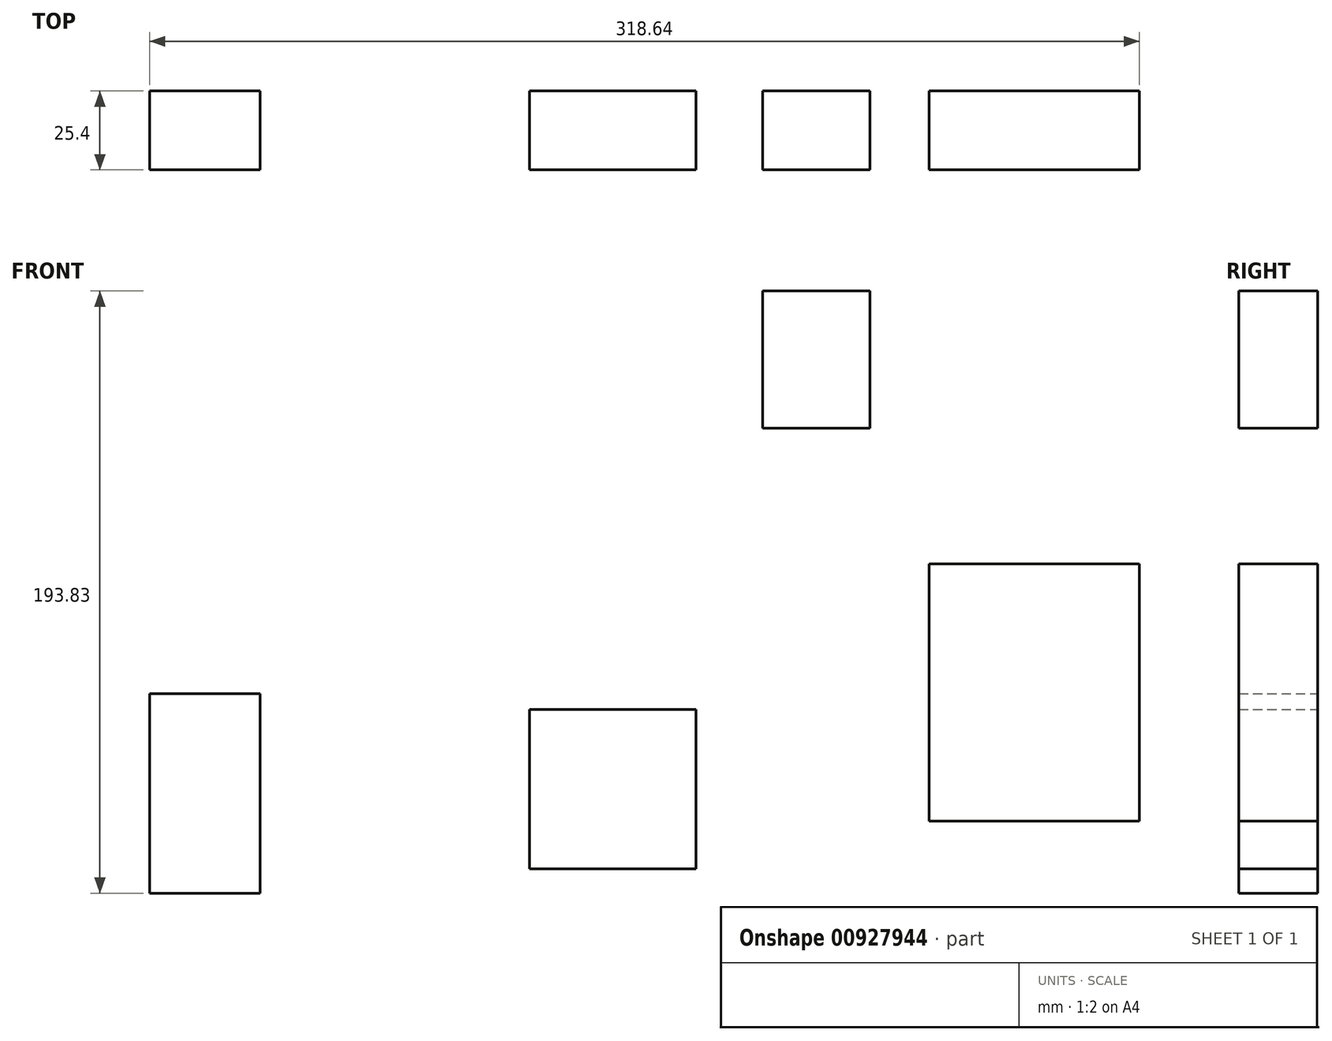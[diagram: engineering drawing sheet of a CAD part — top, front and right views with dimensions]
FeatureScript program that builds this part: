
annotation { "Feature Type Name" : "Feature", "Feature Type Description" : "" }
export const myFeature = defineFeature(function(context is Context, id is Id, definition is map)
    precondition{}
    {
        {
            var Q0;
            Q0=qCreatedBy(makeId("Front.planeOp"),FACE);
            var sketch = newSketch(context, id + "F0", { "sketchPlane" : qUnion([Q0])});
            skLineSegment(sketch, "E0.bottom", {"start": v(-160.88, 19.3) * mm, "end": v(-125.32, 19.3) * mm});
            skLineSegment(sketch, "E0.top", {"start": v(-160.88, -44.97) * mm, "end": v(-125.32, -44.97) * mm});
            skLineSegment(sketch, "E0.left", {"start": v(-160.88, 19.3) * mm, "end": v(-160.88, -44.97) * mm});
            skLineSegment(sketch, "E0.right", {"start": v(-125.32, 19.3) * mm, "end": v(-125.32, -44.97) * mm});
            skLineSegment(sketch, "E1.bottom", {"start": v(-38.6, 14.17) * mm, "end": v(15, 14.17) * mm});
            skLineSegment(sketch, "E1.top", {"start": v(-38.6, -37.11) * mm, "end": v(15, -37.11) * mm});
            skLineSegment(sketch, "E1.left", {"start": v(-38.6, 14.17) * mm, "end": v(-38.6, -37.11) * mm});
            skLineSegment(sketch, "E1.right", {"start": v(15, 14.17) * mm, "end": v(15, -37.11) * mm});
            skLineSegment(sketch, "E2.bottom", {"start": v(90.03, 61.04) * mm, "end": v(157.76, 61.04) * mm});
            skLineSegment(sketch, "E2.top", {"start": v(90.03, -21.72) * mm, "end": v(157.76, -21.72) * mm});
            skLineSegment(sketch, "E2.left", {"start": v(90.03, 61.04) * mm, "end": v(90.03, -21.72) * mm});
            skLineSegment(sketch, "E2.right", {"start": v(157.76, 61.04) * mm, "end": v(157.76, -21.72) * mm});
            skLineSegment(sketch, "E3.bottom", {"start": v(36.44, 148.86) * mm, "end": v(71.03, 148.86) * mm});
            skLineSegment(sketch, "E3.top", {"start": v(36.44, 104.76) * mm, "end": v(71.03, 104.76) * mm});
            skLineSegment(sketch, "E3.left", {"start": v(36.44, 148.86) * mm, "end": v(36.44, 104.76) * mm});
            skLineSegment(sketch, "E3.right", {"start": v(71.03, 148.86) * mm, "end": v(71.03, 104.76) * mm});
            skSolve(sketch);
        }
        {
            var Q0;
            Q0 = qSketchRegion(id + "F0", true);
            extrude(context, id + "F1", {"entities" : qUnion([Q0]), "depth" : 25.4 * mm, "offsetDistance" : 25.4 * mm});
        }
    });
